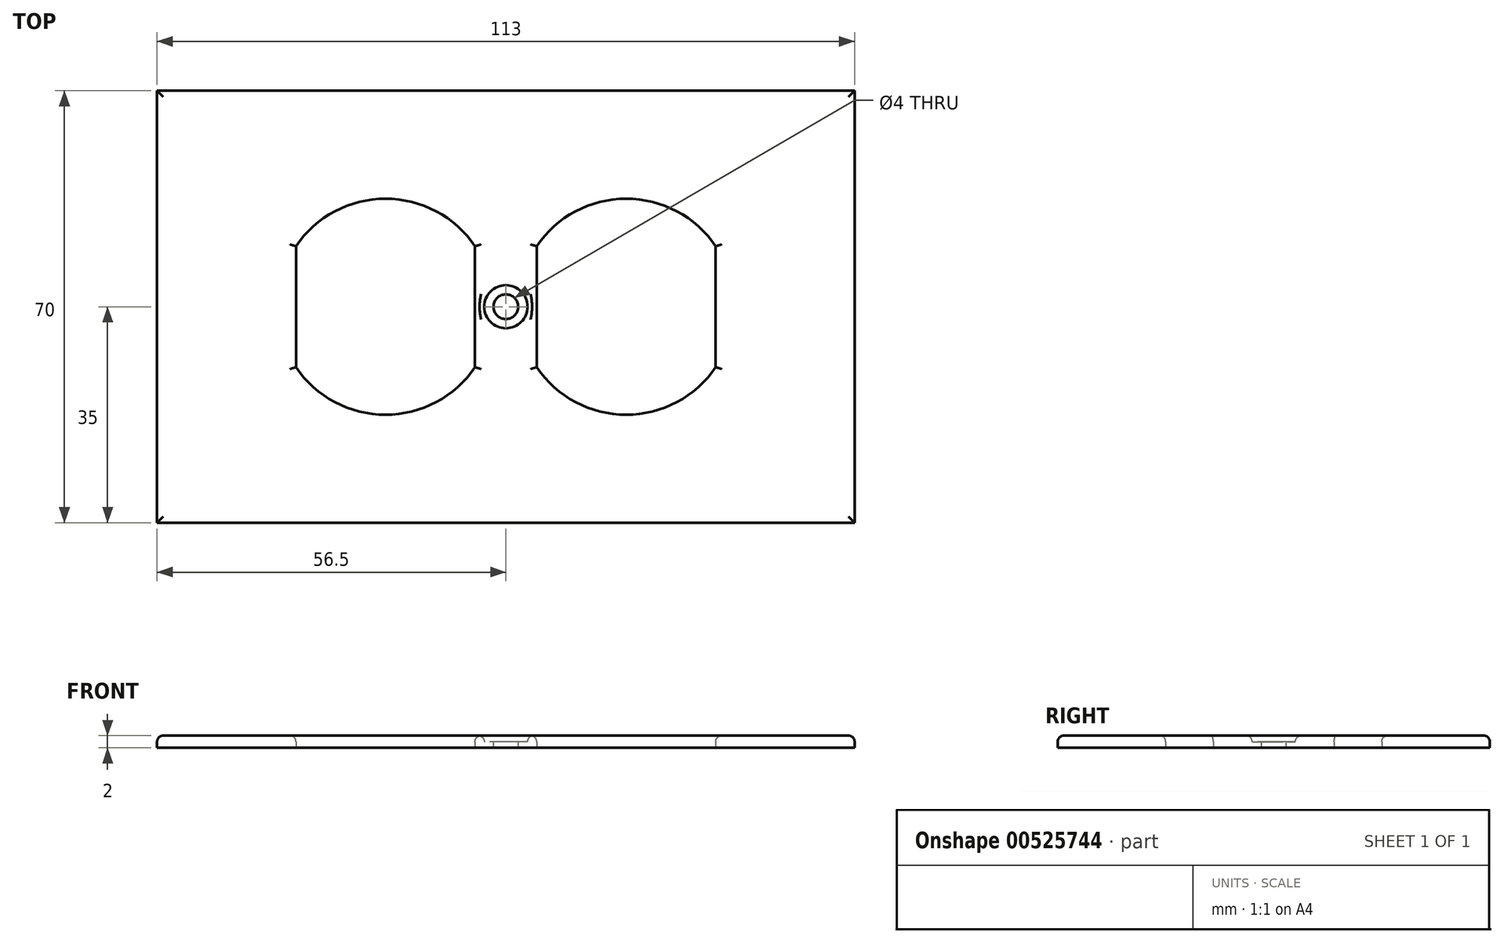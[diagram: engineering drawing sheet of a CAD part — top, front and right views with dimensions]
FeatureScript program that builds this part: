
annotation { "Feature Type Name" : "Feature", "Feature Type Description" : "" }
export const myFeature = defineFeature(function(context is Context, id is Id, definition is map)
    precondition{}
    {
        {
            var Q0;
            Q0=qCreatedBy(makeId("Top.planeOp"),FACE);
            var sketch = newSketch(context, id + "F0", { "sketchPlane" : qUnion([Q0])});
            skLineSegment(sketch, "E0.bottom", {"start": v(56.5, -35) * mm, "end": v(-56.5, -35) * mm});
            skLineSegment(sketch, "E0.top", {"start": v(56.5, 35) * mm, "end": v(-56.5, 35) * mm});
            skLineSegment(sketch, "E0.left", {"start": v(56.5, -35) * mm, "end": v(56.5, 35) * mm});
            skLineSegment(sketch, "E0.right", {"start": v(-56.5, -35) * mm, "end": v(-56.5, 35) * mm});
            skPoint(sketch, "E0.middle", {"position": v(0, 0) * mm});
            skLineSegment(sketch, "E1", {"start": v(-19.5, 0) * mm, "end": v(19.5, 0) * mm, "construction": true});
            skCircle(sketch, "E2", {"center": v(-19.5, 0) * mm, "radius": 17.5 * mm});
            skCircle(sketch, "E3", {"center": v(19.5, 0) * mm, "radius": 17.5 * mm});
            skLineSegment(sketch, "E4.bottom", {"start": v(-5, -9.8) * mm, "end": v(-34, -9.8) * mm, "construction": true});
            skLineSegment(sketch, "E4.top", {"start": v(-5, 9.8) * mm, "end": v(-34, 9.8) * mm, "construction": true});
            skLineSegment(sketch, "E4.left", {"start": v(-5, -9.8) * mm, "end": v(-5, 9.8) * mm});
            skLineSegment(sketch, "E4.right", {"start": v(-34, -9.8) * mm, "end": v(-34, 9.8) * mm});
            skLineSegment(sketch, "E5.bottom", {"start": v(5, -9.8) * mm, "end": v(34, -9.8) * mm, "construction": true});
            skLineSegment(sketch, "E5.top", {"start": v(5, 9.8) * mm, "end": v(34, 9.8) * mm, "construction": true});
            skLineSegment(sketch, "E5.left", {"start": v(5, -9.8) * mm, "end": v(5, 9.8) * mm});
            skLineSegment(sketch, "E5.right", {"start": v(34, -9.8) * mm, "end": v(34, 9.8) * mm});
            skSolve(sketch);
        }
        {
            var Q0;
            Q0=makeQuery(id+"F0.imprint","IMPRINT",FACE,{"disambiguationData":[TD([[makeQuery(id+"F0.imprint","IMPRINT",EDGE,{"derivedFrom":sQuery(id+"F0.wireOp",EDGE,"E0.bottom")}),-1.0]])]});
            var Q1;
            {var subQ0=sQuery(id+"F0.wireOp",EDGE,"E4.right");Q1=makeQuery(id+"F0.imprint","IMPRINT",FACE,{"disambiguationData":[TD([[makeQuery(id+"F0.imprint","IMPRINT",EDGE,{"derivedFrom":subQ0}),1.0]])]});}
            var Q2;
            {var subQ0=sQuery(id+"F0.wireOp",EDGE,"E4.left");Q2=makeQuery(id+"F0.imprint","IMPRINT",FACE,{"disambiguationData":[TD([[makeQuery(id+"F0.imprint","IMPRINT",EDGE,{"derivedFrom":subQ0}),-1.0]])]});}
            var Q3;
            {var subQ0=sQuery(id+"F0.wireOp",EDGE,"E5.left");Q3=makeQuery(id+"F0.imprint","IMPRINT",FACE,{"disambiguationData":[TD([[makeQuery(id+"F0.imprint","IMPRINT",EDGE,{"derivedFrom":subQ0}),1.0]])]});}
            var Q4;
            {var subQ0=sQuery(id+"F0.wireOp",EDGE,"E5.right");Q4=makeQuery(id+"F0.imprint","IMPRINT",FACE,{"disambiguationData":[TD([[makeQuery(id+"F0.imprint","IMPRINT",EDGE,{"derivedFrom":subQ0}),-1.0]])]});}
            extrude(context, id + "F1", {"entities" : qUnion([Q0, Q1, Q2, Q3, Q4]), "depth" : 2 * mm, "offsetDistance" : 25 * mm});
        }
        {
            var Q0;
            Q0=makeQuery(id+"F1.opExtrude","CAP_FACE",FACE,{"disambiguationData":[OSD([sQuery(id+"F0.wireOp",EDGE,"E0.bottom"),sQuery(id+"F0.wireOp",EDGE,"E0.top"),sQuery(id+"F0.wireOp",EDGE,"E0.left"),sQuery(id+"F0.wireOp",EDGE,"E0.right"),sQuery(id+"F0.wireOp",EDGE,"E2"),sQuery(id+"F0.wireOp",EDGE,"E3"),sQuery(id+"F0.wireOp",EDGE,"E4.left"),sQuery(id+"F0.wireOp",EDGE,"E4.right"),sQuery(id+"F0.wireOp",EDGE,"E5.left"),sQuery(id+"F0.wireOp",EDGE,"E5.right")])],"isStart":false});
            var sketch = newSketch(context, id + "F2", { "sketchPlane" : qUnion([Q0])});
            skPoint(sketch, "E6.0", {"position": v(0, 0) * mm});
            skSolve(sketch);
        }
        {
            var Q0;
            Q0=sQuery(id+"F2.wireOp",VERTEX,"E6.0");
            var Q1;
            Q1=makeQuery(id+"F1.opExtrude","SWEPT_BODY",BODY,{"disambiguationData":[OSD([sQuery(id+"F0.wireOp",EDGE,"E0.bottom"),sQuery(id+"F0.wireOp",EDGE,"E0.top"),sQuery(id+"F0.wireOp",EDGE,"E0.left"),sQuery(id+"F0.wireOp",EDGE,"E0.right"),sQuery(id+"F0.wireOp",EDGE,"E2"),sQuery(id+"F0.wireOp",EDGE,"E3"),sQuery(id+"F0.wireOp",EDGE,"E4.left"),sQuery(id+"F0.wireOp",EDGE,"E4.right"),sQuery(id+"F0.wireOp",EDGE,"E5.left"),sQuery(id+"F0.wireOp",EDGE,"E5.right")])]});
            hole(context, id + "F3", {"style" : HoleStyle.C_BORE, "endStyle" : HoleEndStyle.THROUGH, "holeDiameter" : 4 * mm, "cBoreDiameter" : 7 * mm, "cBoreDepth" : 1 * mm, "isTappedThrough" : true, "tappedDepth" : 12 * mm, "tapClearance" : 3, "startFromSketch" : true, "locations" : qUnion([Q0]), "scope" : qUnion([Q1])});
        }
        {
            var Q0;
            Q0=makeQuery(id+"F1.opExtrude","CAP_FACE",FACE,{"disambiguationData":[OSD([sQuery(id+"F0.wireOp",EDGE,"E0.bottom"),sQuery(id+"F0.wireOp",EDGE,"E0.top"),sQuery(id+"F0.wireOp",EDGE,"E0.left"),sQuery(id+"F0.wireOp",EDGE,"E0.right"),sQuery(id+"F0.wireOp",EDGE,"E2"),sQuery(id+"F0.wireOp",EDGE,"E3"),sQuery(id+"F0.wireOp",EDGE,"E4.left"),sQuery(id+"F0.wireOp",EDGE,"E4.right"),sQuery(id+"F0.wireOp",EDGE,"E5.left"),sQuery(id+"F0.wireOp",EDGE,"E5.right")])],"isStart":false});
            fillet(context, id + "F4", {"entities" : qUnion([Q0]), "radius" : 1 * mm, "tangentPropagation" : true, "allowEdgeOverflow" : false});
        }
    });
